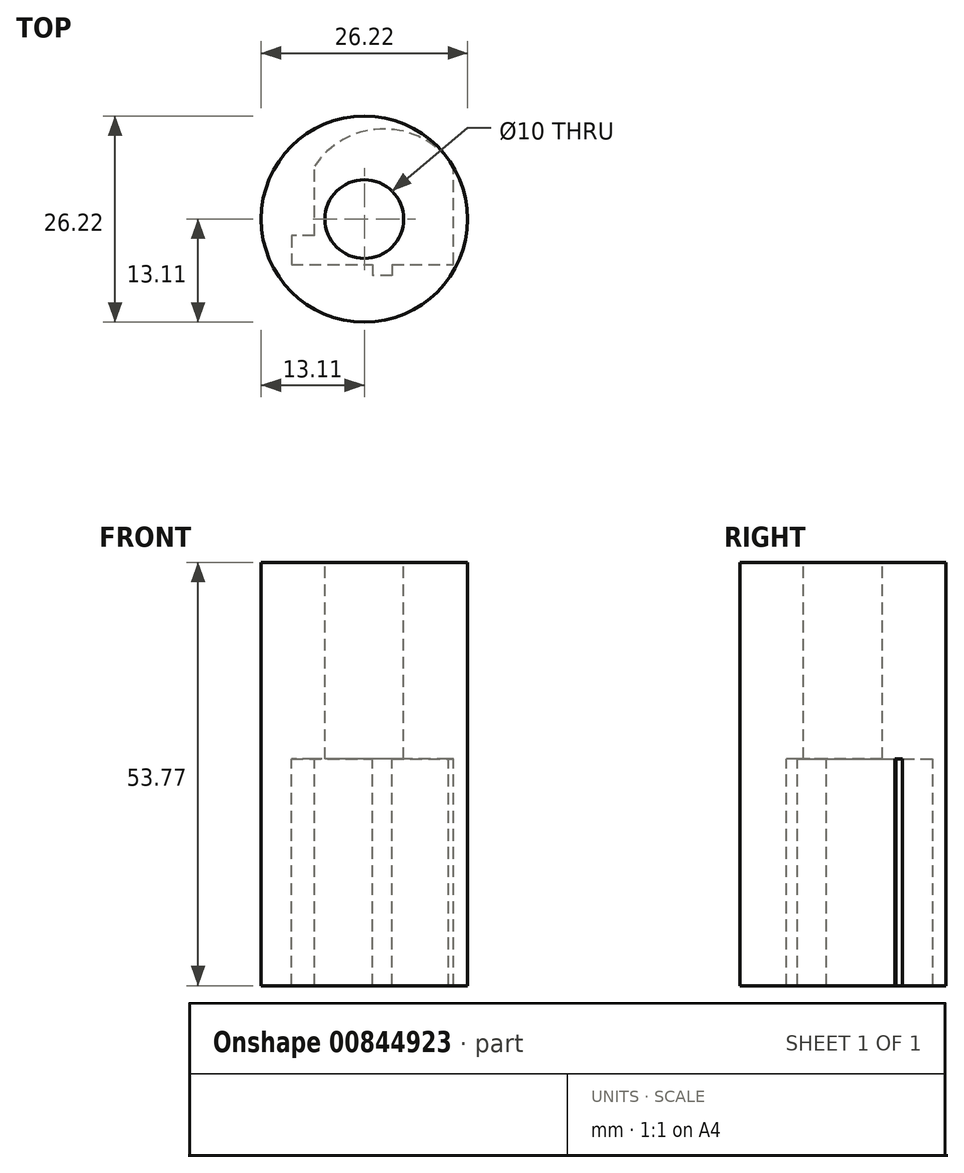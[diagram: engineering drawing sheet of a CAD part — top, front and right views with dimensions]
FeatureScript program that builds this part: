
annotation { "Feature Type Name" : "Feature", "Feature Type Description" : "" }
export const myFeature = defineFeature(function(context is Context, id is Id, definition is map)
    precondition{}
    {
        {
            var Q0;
            Q0=qCreatedBy(makeId("Top.planeOp"),FACE);
            var sketch = newSketch(context, id + "F0", { "sketchPlane" : qUnion([Q0])});
            skCircle(sketch, "E0", {"center": v(0, 0) * mm, "radius": 13.12 * mm, "construction": true});
            skSolve(sketch);
        }
        {
            var Q0;
            Q0=qCreatedBy(makeId("Top.planeOp"),FACE);
            var sketch = newSketch(context, id + "F1", { "sketchPlane" : qUnion([Q0])});
            skCircle(sketch, "E1", {"center": v(0, 0) * mm, "radius": 13.1 * mm});
            skCircle(sketch, "E2", {"center": v(0, 0) * mm, "radius": 5 * mm});
            skCircle(sketch, "E3.0", {"center": v(0, 0) * mm, "radius": 13.12 * mm});
            skSolve(sketch);
        }
        {
            var Q0;
            Q0=makeQuery(id+"F1.imprint","IMPRINT",FACE,{"disambiguationData":[TD([[makeQuery(id+"F1.imprint","IMPRINT",EDGE,{"derivedFrom":sQuery(id+"F1.wireOp",EDGE,"E1")}),1.0]])]});
            extrude(context, id + "F2", {"entities" : qUnion([Q0]), "oppositeDirection" : true, "depth" : 13.77 * mm, "offsetDistance" : 25 * mm, "hasSecondDirection" : true, "secondDirectionOppositeDirection" : false, "secondDirectionDepth" : 40 * mm});
        }
        {
            var Q0;
            Q0=qCreatedBy(makeId("Top.planeOp"),FACE);
            cPlane(context, id + "F3", {"entities" : qUnion([Q0]), "cplaneType" : CPlaneType.OFFSET, "offset" : 15 * mm, "width" : 150 * mm, "height" : 150 * mm});
        }
        {
            var Q0;
            Q0=qCreatedBy(id+"F3.planeOp",FACE);
            var sketch = newSketch(context, id + "F4", { "sketchPlane" : qUnion([Q0])});
            skLineSegment(sketch, "E4.bottom", {"start": v(-9.28, -3.55) * mm, "end": v(11.32, -3.55) * mm});
            skLineSegment(sketch, "E4.top", {"start": v(-9.28, -5.76) * mm, "end": v(11.32, -5.76) * mm});
            skLineSegment(sketch, "E4.left", {"start": v(-9.28, -3.55) * mm, "end": v(-9.28, -5.76) * mm});
            skLineSegment(sketch, "E4.right", {"start": v(11.32, -3.55) * mm, "end": v(11.32, -5.76) * mm});
            skLineSegment(sketch, "E5.0", {"start": v(-6.34, -5.76) * mm, "end": v(1.01, -5.76) * mm});
            skLineSegment(sketch, "E6.top", {"start": v(3.52, -7.17) * mm, "end": v(1.01, -7.17) * mm});
            skLineSegment(sketch, "E6.left", {"start": v(3.52, -5.76) * mm, "end": v(3.52, -7.17) * mm});
            skLineSegment(sketch, "E6.right", {"start": v(1.01, -5.76) * mm, "end": v(1.01, -7.17) * mm});
            skLineSegment(sketch, "E7.0", {"start": v(10.91, -3.55) * mm, "end": v(10.91, -5.76) * mm});
            skLineSegment(sketch, "E8.0", {"start": v(-9.69, -3.55) * mm, "end": v(-9.69, -5.76) * mm});
            skLineSegment(sketch, "E9.top", {"start": v(-9.69, -8.47) * mm, "end": v(-6.34, -8.47) * mm});
            skLineSegment(sketch, "E9.left", {"start": v(-9.69, -5.76) * mm, "end": v(-9.69, -8.47) * mm});
            skLineSegment(sketch, "E9.right", {"start": v(-6.34, -5.76) * mm, "end": v(-6.34, -8.47) * mm});
            skLineSegment(sketch, "E10.trimOffspring", {"start": v(3.52, -5.76) * mm, "end": v(10.91, -5.76) * mm});
            skLineSegment(sketch, "E11.bottom", {"start": v(-6.34, -3.55) * mm, "end": v(-9.28, -3.55) * mm});
            skLineSegment(sketch, "E11.top", {"start": v(-6.34, -2.11) * mm, "end": v(-9.28, -2.11) * mm});
            skLineSegment(sketch, "E11.left", {"start": v(-6.34, -3.55) * mm, "end": v(-6.34, -2.11) * mm});
            skLineSegment(sketch, "E11.right", {"start": v(-9.28, -3.55) * mm, "end": v(-9.28, -2.11) * mm});
            skLineSegment(sketch, "E12.bottom", {"start": v(11.32, -3.55) * mm, "end": v(-6.34, -3.55) * mm});
            skLineSegment(sketch, "E12.top", {"start": v(11.32, 6.73) * mm, "end": v(-6.34, 6.73) * mm});
            skLineSegment(sketch, "E12.left", {"start": v(11.32, -3.55) * mm, "end": v(11.32, 6.73) * mm});
            skLineSegment(sketch, "E12.right", {"start": v(-6.34, -3.55) * mm, "end": v(-6.34, 6.73) * mm});
            skArc(sketch, "E13", {"start": v(11.32, 6.73) * mm, "mid": v(2.5, 11.44) * mm, "end": v(-6.34, 6.73) * mm});
            skSolve(sketch);
        }
        {
            var Q0;
            {var subQ1=sQuery(id+"F4.wireOp",EDGE,"E4.right");var subQ9=sQuery(id+"F4.wireOp",EDGE,"E11.left");var subQ12=sQuery(id+"F4.wireOp",EDGE,"E4.left");var subQ14=makeQuery(id+"F4.imprint","IMPRINT",EDGE,{"derivedFrom":subQ9});var subQ15=makeQuery(id+"F4.imprint","IMPRINT",EDGE,{"derivedFrom":sQuery(id+"F4.wireOp",EDGE,"E12.top")});Q0=qUnion([makeQuery(id+"F4.imprint","IMPRINT",FACE,{"disambiguationData":[TD([[makeQuery(id+"F4.imprint","IMPRINT",EDGE,{"derivedFrom":sQuery(id+"F4.wireOp",EDGE,"E6.top")}),-1.0]])]}),makeQuery(id+"F4.imprint","IMPRINT",FACE,{"disambiguationData":[TD([[makeQuery(id+"F4.imprint","IMPRINT",EDGE,{"derivedFrom":subQ12}),1.0]])]}),makeQuery(id+"F4.imprint","IMPRINT",FACE,{"disambiguationData":[TD([[subQ15,-1.0]])]}),makeQuery(id+"F4.imprint","IMPRINT",FACE,{"disambiguationData":[TD([[subQ14,-1.0]])]}),makeQuery(id+"F4.imprint","IMPRINT",FACE,{"disambiguationData":[TD([[makeQuery(id+"F4.imprint","IMPRINT",EDGE,{"derivedFrom":sQuery(id+"F4.wireOp",EDGE,"E11.top")}),1.0]])]}),makeQuery(id+"F4.imprint","IMPRINT",FACE,{"disambiguationData":[TD([[makeQuery(id+"F4.imprint","IMPRINT",EDGE,{"derivedFrom":subQ1}),-1.0]])]})]);}
            extrude(context, id + "F5", {"entities" : qUnion([Q0]), "operationType" : NewBodyOperationType.REMOVE, "oppositeDirection" : true, "depth" : 28.77 * mm, "offsetDistance" : 25 * mm});
        }
    });
